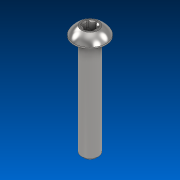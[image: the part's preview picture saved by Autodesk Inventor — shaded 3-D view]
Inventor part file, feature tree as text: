
AUTODESK INVENTOR PART (.ipt)
format: ipt  version: 2022.2 (Build 262287000, 287)  size: 173,568 bytes
history: native  units: in
note: dims shown in document units (in); Inventor stores cm internally (conversion verified against a paired STEP export)
features: direct_edit x1, chamfer x1, move_body x1
ambient origin geometry x8: Origin, YZ Plane, XZ Plane, XY Plane, X Axis, Y Axis, Z Axis, Center Point
bodies: Solid1 (feature_tree)
feature tree (3):
  direct_edit  "Direct Edit1"
  chamfer  "Chamfer2"  [1 undecoded]
  move_body  "Move1"
note: 1 required parameter value undecoded (feature->parameter linkage not recoverable at this tier; creation-order binding heuristic only, values carry confidence <= 0.55)
